# Revit family: GBVK22TZV05
name_source: partatom
category: Allgemeines Modell
units: mm (PartAtom-declared; Revit-internal decimal feet)

## family parameters
Arbeitsebenenbasiert = Nein
Beim Laden mit Abzugskörper schneiden = Nein
Bemaßung runder Anschluss = Durchmesser verwenden
Beschriftungsausrichtung beibehalten = Nein
Gemeinsam genutzt = Nein
Immer vertikal = Ja
Kann Basisbauteil für Bewehrung sein = Nein
Raumberechnungspunkt = Nein
Teiletyp = Normal

## types (1)
- GBVK22TZV05
    Bauteilnummer = GBVK22TZV05
    DocNumber = GBVK22TZV05.ipt
    Erstellungsdatum = 14.01.2019
    Folder = ARTIKEL\G1_Abstandhalter\G1C_Mauerstärke\FBVK%\
    Genehmigungsdatum Konstr. = 09.03.2022
    Gewicht = 0.05
    Kennung = Artikel
    Konstruktionsstatus = 1
    Revisionsnummer = -
    Status = Freigegeben
    VDS_Category = 3D-Konstruktion Bauteil
    Vorgabe-Ansicht = 0 mm  [stored 0 ft]

note: [stored X ft] marks values corroborated as IEEE doubles in the binary element streams (Revit-internal decimal feet)
